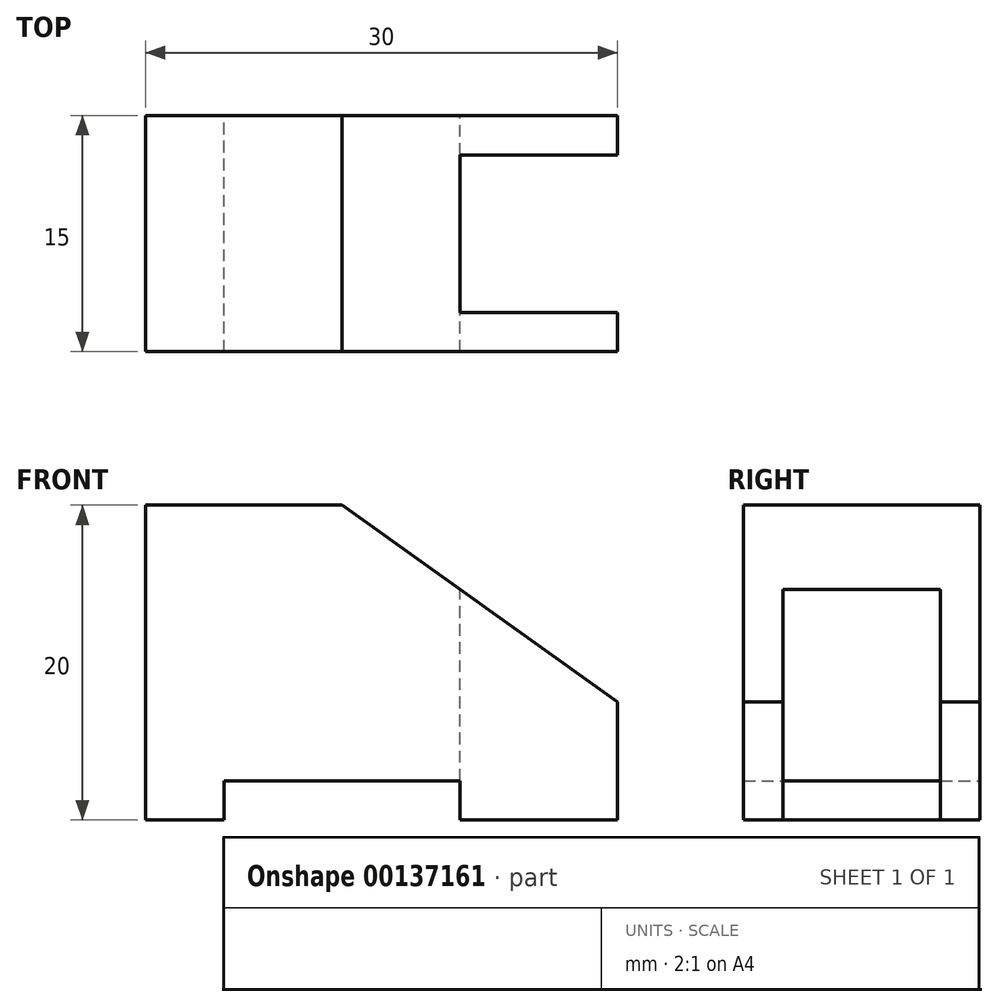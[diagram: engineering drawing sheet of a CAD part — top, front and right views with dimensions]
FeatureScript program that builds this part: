
annotation { "Feature Type Name" : "Feature", "Feature Type Description" : "" }
export const myFeature = defineFeature(function(context is Context, id is Id, definition is map)
    precondition{}
    {
        {
            var Q0;
            Q0=qCreatedBy(makeId("Front.planeOp"),FACE);
            var sketch = newSketch(context, id + "F0", { "sketchPlane" : qUnion([Q0])});
            skLineSegment(sketch, "E0", {"start": v(0, 0) * mm, "end": v(0, 20) * mm});
            skLineSegment(sketch, "E1", {"start": v(0, 20) * mm, "end": v(12.5, 20) * mm});
            skLineSegment(sketch, "E2", {"start": v(0, 0) * mm, "end": v(5, 0) * mm});
            skLineSegment(sketch, "E3", {"start": v(5, 0) * mm, "end": v(5, 2.5) * mm});
            skLineSegment(sketch, "E4", {"start": v(5, 2.5) * mm, "end": v(20, 2.5) * mm});
            skLineSegment(sketch, "E5", {"start": v(20, 2.5) * mm, "end": v(20, 0) * mm});
            skLineSegment(sketch, "E6", {"start": v(20, 0) * mm, "end": v(30, 0) * mm});
            skLineSegment(sketch, "E7", {"start": v(30, 0) * mm, "end": v(30, 7.5) * mm});
            skLineSegment(sketch, "E8", {"start": v(30, 7.5) * mm, "end": v(12.5, 20) * mm});
            skSolve(sketch);
        }
        {
            var Q0;
            Q0=makeQuery(id+"F0.imprint","IMPRINT",FACE,{"disambiguationData":[TD([[makeQuery(id+"F0.imprint","IMPRINT",EDGE,{"derivedFrom":sQuery(id+"F0.wireOp",EDGE,"E0")}),-1.0]])]});
            extrude(context, id + "F1", {"entities" : qUnion([Q0]), "depth" : 15 * mm});
        }
        {
            var Q0;
            Q0=makeQuery(id+"F1.opExtrude","CAP_FACE",FACE,{"disambiguationData":[OSD([sQuery(id+"F0.wireOp",EDGE,"E0"),sQuery(id+"F0.wireOp",EDGE,"E1"),sQuery(id+"F0.wireOp",EDGE,"E2"),sQuery(id+"F0.wireOp",EDGE,"E3"),sQuery(id+"F0.wireOp",EDGE,"E4"),sQuery(id+"F0.wireOp",EDGE,"E5"),sQuery(id+"F0.wireOp",EDGE,"E6"),sQuery(id+"F0.wireOp",EDGE,"E7"),sQuery(id+"F0.wireOp",EDGE,"E8")])],"isStart":false});
            var sketch = newSketch(context, id + "F2", { "sketchPlane" : qUnion([Q0])});
            skLineSegment(sketch, "E9", {"start": v(20, 2.5) * mm, "end": v(20, 14.64) * mm});
            skLineSegment(sketch, "E10", {"start": v(20, 14.64) * mm, "end": v(30, 7.5) * mm});
            skLineSegment(sketch, "E11", {"start": v(30, 7.5) * mm, "end": v(30, 0) * mm});
            skLineSegment(sketch, "E12", {"start": v(30, 0) * mm, "end": v(20, 0) * mm});
            skLineSegment(sketch, "E13", {"start": v(20, 0) * mm, "end": v(20, 2.5) * mm});
            skSolve(sketch);
        }
        {
            var Q0;
            Q0 = qSketchRegion(id + "F2", true);
            var Q1;
            Q1=makeQuery(id+"F2.imprint","IMPRINT",FACE,{"disambiguationData":[TD([[makeQuery(id+"F2.imprint","IMPRINT",EDGE,{"derivedFrom":sQuery(id+"F2.wireOp",EDGE,"E9")}),-1.0]])]});
            extrude(context, id + "F3", {"entities" : qUnion([Q0, Q1]), "operationType" : NewBodyOperationType.REMOVE, "oppositeDirection" : true, "depth" : 12.5 * mm, "hasSecondDirection" : true, "secondDirectionOppositeDirection" : true, "secondDirectionDepth" : 2.5 * mm});
        }
    });
